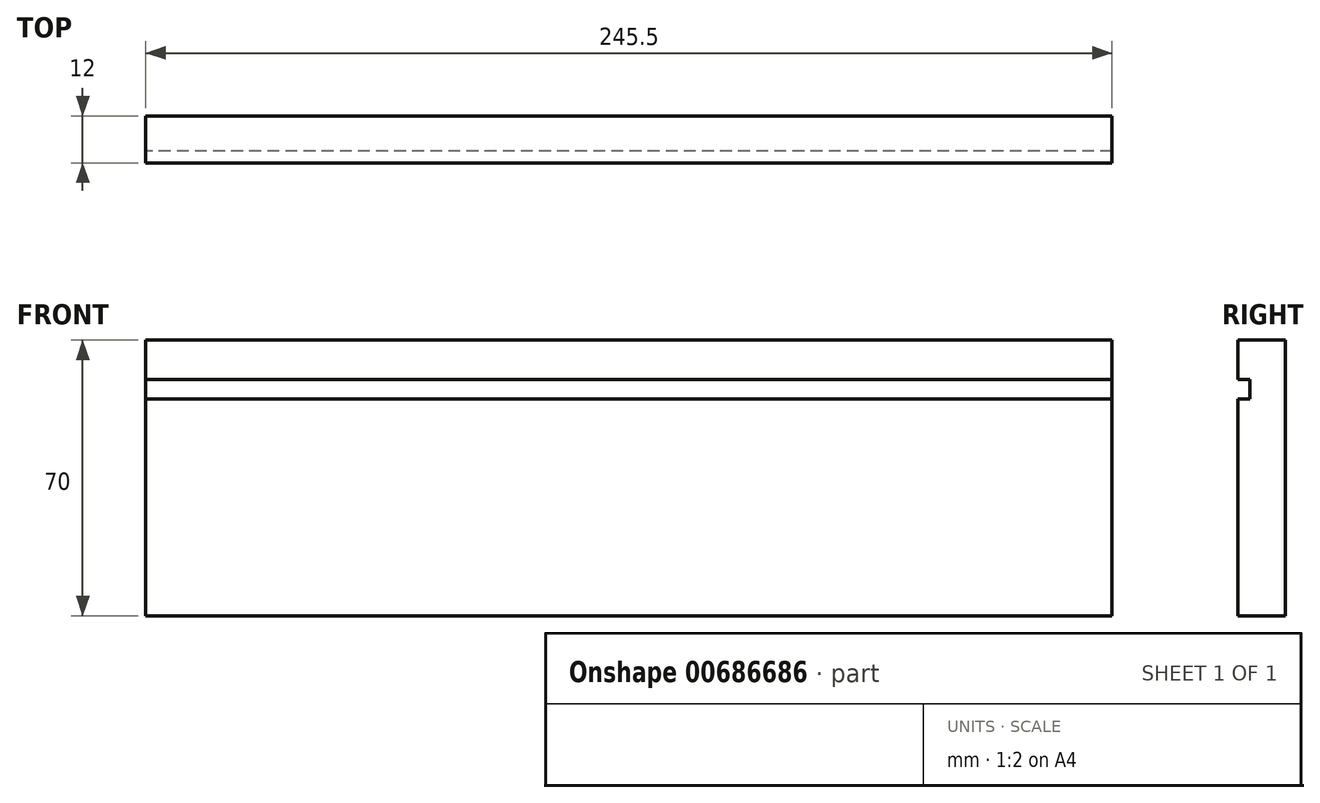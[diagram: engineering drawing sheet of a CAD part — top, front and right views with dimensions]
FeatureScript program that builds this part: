
annotation { "Feature Type Name" : "Feature", "Feature Type Description" : "" }
export const myFeature = defineFeature(function(context is Context, id is Id, definition is map)
    precondition{}
    {
        {
            var Q0;
            Q0=qCreatedBy(makeId("Right.planeOp"),FACE);
            var sketch = newSketch(context, id + "F0", { "sketchPlane" : qUnion([Q0])});
            skLineSegment(sketch, "E0.bottom", {"start": v(0, 0) * mm, "end": v(12, 0) * mm});
            skLineSegment(sketch, "E0.top", {"start": v(0, 70) * mm, "end": v(12, 70) * mm});
            skLineSegment(sketch, "E0.left", {"start": v(0, 0) * mm, "end": v(0, 55) * mm});
            skLineSegment(sketch, "E0.right", {"start": v(12, 0) * mm, "end": v(12, 70) * mm});
            skLineSegment(sketch, "E1.bottom", {"start": v(0, 60) * mm, "end": v(3, 60) * mm});
            skLineSegment(sketch, "E1.top", {"start": v(0, 55) * mm, "end": v(3, 55) * mm});
            skLineSegment(sketch, "E1.right", {"start": v(3, 60) * mm, "end": v(3, 55) * mm});
            skLineSegment(sketch, "E2.trimOffspring", {"start": v(0, 60) * mm, "end": v(0, 70) * mm});
            skSolve(sketch);
        }
        {
            var Q0;
            Q0=qSketchRegion(id+"F0",true);
            extrude(context, id + "F1", {"entities" : qUnion([Q0]), "depth" : 245.5 * mm, "offsetDistance" : 25 * mm});
        }
    });
